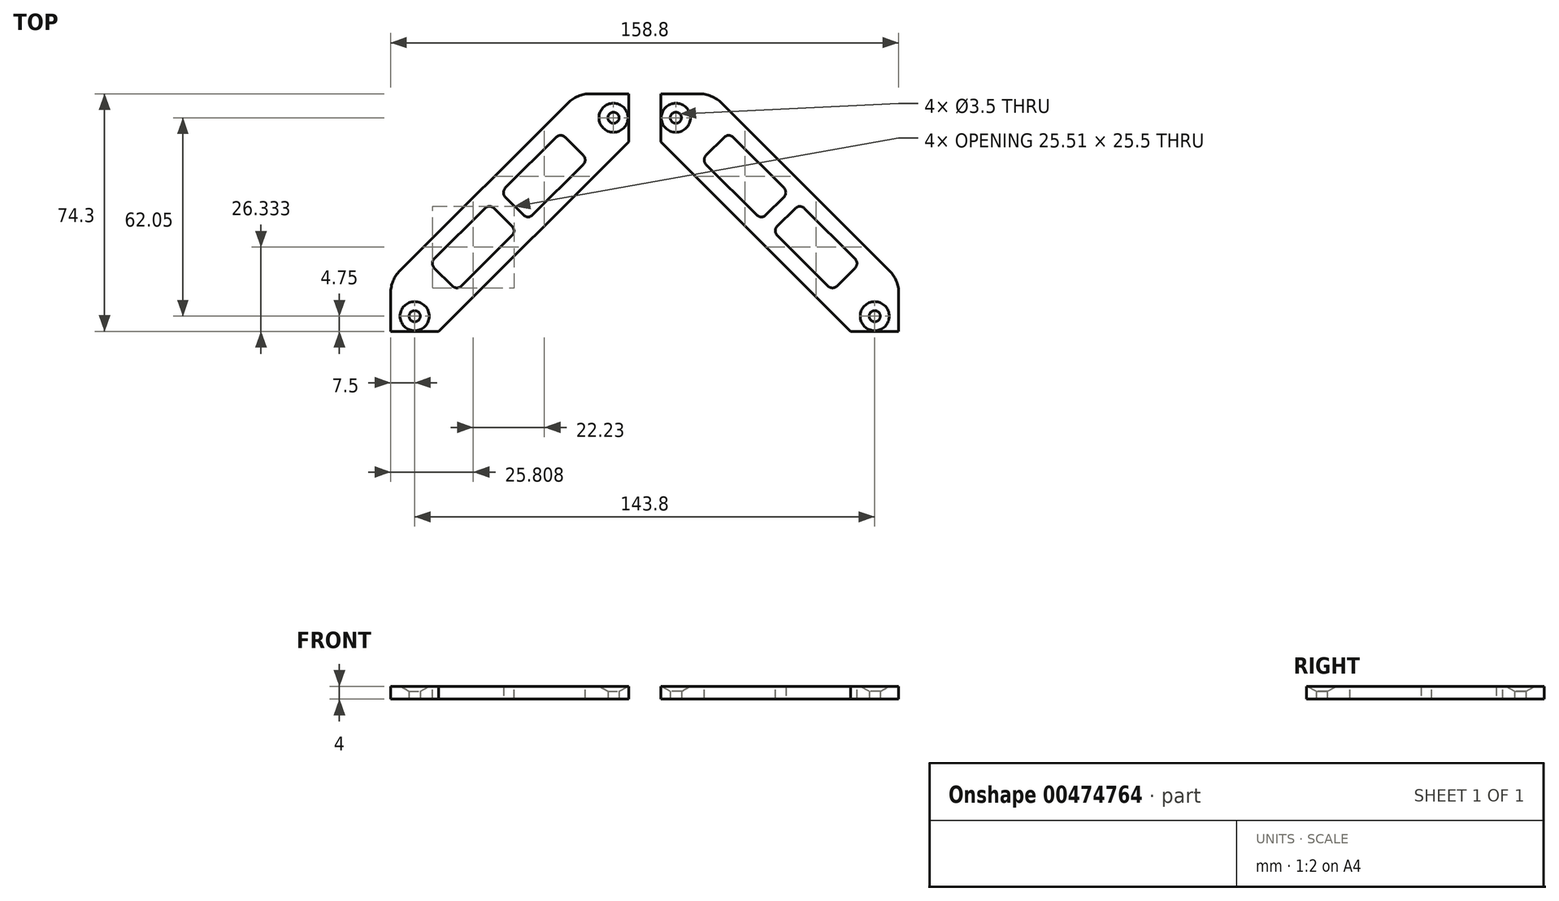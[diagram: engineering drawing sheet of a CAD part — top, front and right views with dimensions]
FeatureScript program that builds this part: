
annotation { "Feature Type Name" : "Feature", "Feature Type Description" : "" }
export const myFeature = defineFeature(function(context is Context, id is Id, definition is map)
    precondition{}
    {
        {
            var Q0;
            Q0=qCreatedBy(makeId("Top.planeOp"),FACE);
            var sketch = newSketch(context, id + "F0", { "sketchPlane" : qUnion([Q0])});
            skLineSegment(sketch, "E0.bottom", {"start": v(0, 0) * mm, "end": v(9.5, 0) * mm, "construction": true});
            skLineSegment(sketch, "E0.top", {"start": v(0, -15) * mm, "end": v(9.5, -15) * mm, "construction": true});
            skLineSegment(sketch, "E0.left", {"start": v(0, 0) * mm, "end": v(0, -15) * mm});
            skLineSegment(sketch, "E0.right", {"start": v(9.5, 0) * mm, "end": v(9.5, -15) * mm, "construction": true});
            skLineSegment(sketch, "E1.bottom", {"start": v(59.4, -64.8) * mm, "end": v(74.4, -64.8) * mm, "construction": true});
            skLineSegment(sketch, "E1.top", {"start": v(59.4, -74.3) * mm, "end": v(74.4, -74.3) * mm});
            skLineSegment(sketch, "E1.left", {"start": v(59.4, -64.8) * mm, "end": v(59.4, -74.3) * mm, "construction": true});
            skLineSegment(sketch, "E1.right", {"start": v(74.4, -64.8) * mm, "end": v(74.4, -74.3) * mm, "construction": true});
            skCircle(sketch, "E2", {"center": v(4.75, -7.5) * mm, "radius": 1.75 * mm});
            skCircle(sketch, "E3", {"center": v(66.9, -69.55) * mm, "radius": 1.75 * mm});
            skLineSegment(sketch, "E4", {"start": v(0, -15) * mm, "end": v(59.4, -74.3) * mm});
            skLineSegment(sketch, "E5", {"start": v(0, 0) * mm, "end": v(16.11, 0) * mm});
            skLineSegment(sketch, "E6", {"start": v(16.11, 0) * mm, "end": v(74.4, -58.19) * mm});
            skLineSegment(sketch, "E7", {"start": v(74.4, -58.19) * mm, "end": v(74.4, -74.3) * mm});
            skLineSegment(sketch, "E8", {"start": v(12.78, -20.7) * mm, "end": v(21.26, -12.2) * mm});
            skLineSegment(sketch, "E9", {"start": v(21.26, -12.2) * mm, "end": v(39.95, -30.86) * mm});
            skLineSegment(sketch, "E10", {"start": v(62.18, -53.05) * mm, "end": v(53.7, -61.54) * mm});
            skLineSegment(sketch, "E11", {"start": v(53.7, -61.54) * mm, "end": v(35, -42.88) * mm});
            skLineSegment(sketch, "E12", {"start": v(33.24, -41.12) * mm, "end": v(41.72, -32.62) * mm, "construction": true});
            skLineSegment(sketch, "E13", {"start": v(31.47, -39.35) * mm, "end": v(39.95, -30.86) * mm});
            skLineSegment(sketch, "E14", {"start": v(35, -42.88) * mm, "end": v(43.49, -34.4) * mm});
            skLineSegment(sketch, "E15.trimOffspring", {"start": v(43.49, -34.4) * mm, "end": v(62.18, -53.05) * mm});
            skLineSegment(sketch, "E16.trimOffspring", {"start": v(31.47, -39.35) * mm, "end": v(12.78, -20.7) * mm});
            skSolve(sketch);
        }
        {
            var Q0;
            Q0 = qSketchRegion(id + "F0", true);
            extrude(context, id + "F1", {"entities" : qUnion([Q0]), "depth" : 4 * mm, "offsetDistance" : 25 * mm});
        }
        {
            var Q0;
            Q0=makeQuery(id+"F1.opExtrude","SWEPT_EDGE",EDGE,{"disambiguationData":[OSD([sQuery(id+"F0.wireOp",EDGE,"E5"),sQuery(id+"F0.wireOp",EDGE,"E6")])]});
            var Q1;
            Q1=makeQuery(id+"F1.opExtrude","SWEPT_EDGE",EDGE,{"disambiguationData":[OSD([sQuery(id+"F0.wireOp",EDGE,"E6"),sQuery(id+"F0.wireOp",EDGE,"E7")])]});
            fillet(context, id + "F2", {"entities" : qUnion([Q0, Q1]), "radius" : 10 * mm, "tangentPropagation" : true, "allowEdgeOverflow" : false});
        }
        {
            var Q0;
            Q0=makeQuery(id+"F1.opExtrude","SWEPT_EDGE",EDGE,{"disambiguationData":[OSD([sQuery(id+"F0.wireOp",EDGE,"E8"),sQuery(id+"F0.wireOp",EDGE,"E9")])]});
            var Q1;
            Q1=makeQuery(id+"F1.opExtrude","SWEPT_EDGE",EDGE,{"disambiguationData":[OSD([sQuery(id+"F0.wireOp",EDGE,"E8"),sQuery(id+"F0.wireOp",EDGE,"E16.trimOffspring")])]});
            var Q2;
            Q2=makeQuery(id+"F1.opExtrude","SWEPT_EDGE",EDGE,{"disambiguationData":[OSD([sQuery(id+"F0.wireOp",EDGE,"E9"),sQuery(id+"F0.wireOp",EDGE,"E13")])]});
            var Q3;
            Q3=makeQuery(id+"F1.opExtrude","SWEPT_EDGE",EDGE,{"disambiguationData":[OSD([sQuery(id+"F0.wireOp",EDGE,"E13"),sQuery(id+"F0.wireOp",EDGE,"E16.trimOffspring")])]});
            var Q4;
            Q4=makeQuery(id+"F1.opExtrude","SWEPT_EDGE",EDGE,{"disambiguationData":[OSD([sQuery(id+"F0.wireOp",EDGE,"E10"),sQuery(id+"F0.wireOp",EDGE,"E11")])]});
            var Q5;
            Q5=makeQuery(id+"F1.opExtrude","SWEPT_EDGE",EDGE,{"disambiguationData":[OSD([sQuery(id+"F0.wireOp",EDGE,"E10"),sQuery(id+"F0.wireOp",EDGE,"E15.trimOffspring")])]});
            var Q6;
            Q6=makeQuery(id+"F1.opExtrude","SWEPT_EDGE",EDGE,{"disambiguationData":[OSD([sQuery(id+"F0.wireOp",EDGE,"E14"),sQuery(id+"F0.wireOp",EDGE,"E15.trimOffspring")])]});
            var Q7;
            Q7=makeQuery(id+"F1.opExtrude","SWEPT_EDGE",EDGE,{"disambiguationData":[OSD([sQuery(id+"F0.wireOp",EDGE,"E11"),sQuery(id+"F0.wireOp",EDGE,"E14")])]});
            fillet(context, id + "F3", {"entities" : qUnion([Q0, Q1, Q2, Q3, Q4, Q5, Q6, Q7]), "radius" : 2 * mm, "tangentPropagation" : true, "allowEdgeOverflow" : false});
        }
        {
            var Q0;
            Q0=makeQuery(id+"F1.opExtrude","CAP_EDGE",EDGE,{"disambiguationData":[OSD([sQuery(id+"F0.wireOp",EDGE,"E2")])],"isStart":false});
            var Q1;
            Q1=makeQuery(id+"F1.opExtrude","CAP_EDGE",EDGE,{"disambiguationData":[OSD([sQuery(id+"F0.wireOp",EDGE,"E3")])],"isStart":false});
            chamfer(context, id + "F4", {"entities" : qUnion([Q0, Q1]), "chamferType" : ChamferType.TWO_OFFSETS, "width1" : 2.8 * mm, "oppositeDirection" : false, "width2" : 1.6 * mm, "tangentPropagation" : true});
        }
        {
            var Q0;
            Q0=qCreatedBy(makeId("Right.planeOp"),FACE);
            cPlane(context, id + "F5", {"entities" : qUnion([Q0]), "cplaneType" : CPlaneType.OFFSET, "offset" : 5 * mm, "oppositeDirection" : true, "width" : 150 * mm, "height" : 150 * mm});
        }
        {
            var Q0;
            Q0=makeQuery(id+"F1.opExtrude","SWEPT_BODY",BODY,{"disambiguationData":[OSD([sQuery(id+"F0.wireOp",EDGE,"E0.left"),sQuery(id+"F0.wireOp",EDGE,"E1.top"),sQuery(id+"F0.wireOp",EDGE,"E2"),sQuery(id+"F0.wireOp",EDGE,"E3"),sQuery(id+"F0.wireOp",EDGE,"E4"),sQuery(id+"F0.wireOp",EDGE,"E5"),sQuery(id+"F0.wireOp",EDGE,"E6"),sQuery(id+"F0.wireOp",EDGE,"E7"),sQuery(id+"F0.wireOp",EDGE,"E8"),sQuery(id+"F0.wireOp",EDGE,"E9"),sQuery(id+"F0.wireOp",EDGE,"E10"),sQuery(id+"F0.wireOp",EDGE,"E11"),sQuery(id+"F0.wireOp",EDGE,"E13"),sQuery(id+"F0.wireOp",EDGE,"E14"),sQuery(id+"F0.wireOp",EDGE,"E15.trimOffspring"),sQuery(id+"F0.wireOp",EDGE,"E16.trimOffspring")])]});
            var Q1;
            Q1=qCreatedBy(id+"F5.planeOp",FACE);
            mirror(context, id + "F6", {"entities" : qUnion([Q0]), "mirrorPlane" : qUnion([Q1])});
        }
    });
